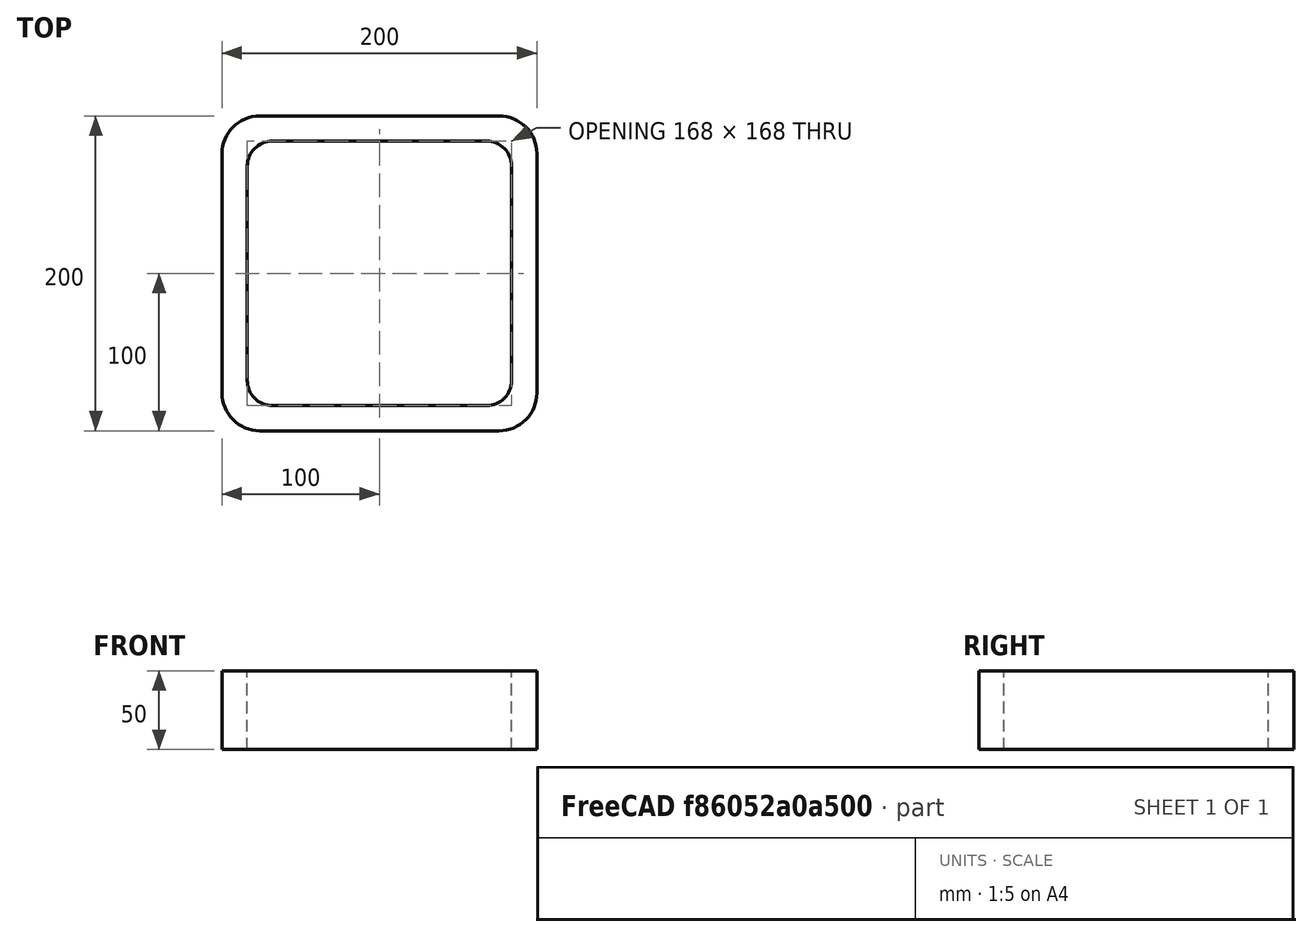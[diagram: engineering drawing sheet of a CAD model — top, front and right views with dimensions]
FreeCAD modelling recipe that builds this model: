
FCSTD DOCUMENT  (FreeCAD 0.15R4671 (Git))
Label: Square hollow section 200x200x16 EN10219 S235JRH
License: All rights reserved
LicenseURL: http://en.wikipedia.org/wiki/All_rights_reserved
objects: Sketcher::SketchObject×1, Part::Extrusion×1
note: 2 computed .brp shape members not serialized (recipe doc carries the construction recipe); baked Part::Feature solids carry a one-line shape summary decoded from their .brp

FEATURE [Sketcher::SketchObject] Sketch
  sketch-geometry (16):
    g0: LineSegment StartX=-68 StartY=84 StartZ=0 EndX=68 EndY=84 EndZ=0
    g1: LineSegment StartX=84 StartY=68 StartZ=0 EndX=84 EndY=-68 EndZ=0
    g2: LineSegment StartX=68 StartY=-84 StartZ=0 EndX=-68 EndY=-84 EndZ=0
    g3: LineSegment StartX=-84 StartY=-68 StartZ=0 EndX=-84 EndY=68 EndZ=0
    g4: LineSegment StartX=-76 StartY=100 StartZ=0 EndX=76 EndY=100 EndZ=0
    g5: LineSegment StartX=100 StartY=76 StartZ=0 EndX=100 EndY=-76 EndZ=0
    g6: LineSegment StartX=76 StartY=-100 StartZ=0 EndX=-76 EndY=-100 EndZ=0
    g7: LineSegment StartX=-100 StartY=-76 StartZ=0 EndX=-100 EndY=76 EndZ=0
    g8: ArcOfCircle CenterX=-68 CenterY=68 CenterZ=0 NormalX=0 NormalY=0 NormalZ=1 Radius=16 StartAngle=1.5708 EndAngle=3.14159
    g9: ArcOfCircle CenterX=68 CenterY=68 CenterZ=0 NormalX=0 NormalY=0 NormalZ=1 Radius=16 StartAngle=0 EndAngle=1.5708
    g10: ArcOfCircle CenterX=68 CenterY=-68 CenterZ=0 NormalX=0 NormalY=0 NormalZ=1 Radius=16 StartAngle=4.71239 EndAngle=6.28319
    g11: ArcOfCircle CenterX=-68 CenterY=-68 CenterZ=0 NormalX=0 NormalY=0 NormalZ=1 Radius=16 StartAngle=3.14159 EndAngle=4.71239
    g12: ArcOfCircle CenterX=76 CenterY=76 CenterZ=0 NormalX=0 NormalY=0 NormalZ=1 Radius=24 StartAngle=0 EndAngle=1.5708
    g13: ArcOfCircle CenterX=76 CenterY=-76 CenterZ=0 NormalX=0 NormalY=0 NormalZ=1 Radius=24 StartAngle=4.71239 EndAngle=6.28319
    g14: ArcOfCircle CenterX=-76 CenterY=-76 CenterZ=0 NormalX=0 NormalY=0 NormalZ=1 Radius=24 StartAngle=3.14159 EndAngle=4.71239
    g15: ArcOfCircle CenterX=-76 CenterY=76 CenterZ=0 NormalX=0 NormalY=0 NormalZ=1 Radius=24 StartAngle=1.5708 EndAngle=3.14159
  constraints (36):
    c: Horizontal(g2)
    c: Vertical(g3)
    c: Horizontal(g6)
    c: Vertical(g7)
    c: Tangent(g3,g8) = 1.5708
    c: Tangent(g0,g8) = 1.5708
    c: Tangent(g0,g9) = 1.5708
    c: Tangent(g1,g9) = 1.5708
    c: Tangent(g1,g10) = 1.5708
    c: Tangent(g2,g10) = 1.5708
    c: Tangent(g2,g11) = 1.5708
    c: Tangent(g3,g11) = 1.5708
    c: Tangent(g4,g12) = 1.5708
    c: Tangent(g5,g12) = 1.5708
    c: Tangent(g5,g13) = 1.5708
    c: Tangent(g6,g13) = 1.5708
    c: Tangent(g6,g14) = 1.5708
    c: Tangent(g7,g14) = 1.5708
    c: Tangent(g7,g15) = 1.5708
    c: Tangent(g4,g15) = 1.5708
    c: Equal(g9,g8)
    c: Equal(g9,g11)
    c: Equal(g9,g10)
    c: Equal(g12,g15)
    c: Equal(g12,g14)
    c: Equal(g12,g13)
    c: Symmetric(g4,g6,g-1)
    c: Symmetric(g7,g5,g-2)
    c: DistanceY(g4,g6) = -200
    c: DistanceX(g7,g5) = 200
    c: Symmetric(g3,g1,g-2)
    c: Symmetric(g0,g2,g-1)
    c: DistanceY(g0,g4) = 16
    c: DistanceX(g5,g1) = -16
    c: Radius(g9) = 16
    c: Radius(g12) = 24
FEATURE [Part::Extrusion] Extrude  label="Square hollow section 200x200x16 EN10219 S235JRH"
  Base = -> Sketch
  Dir = (0,0,50)
  Solid = true
